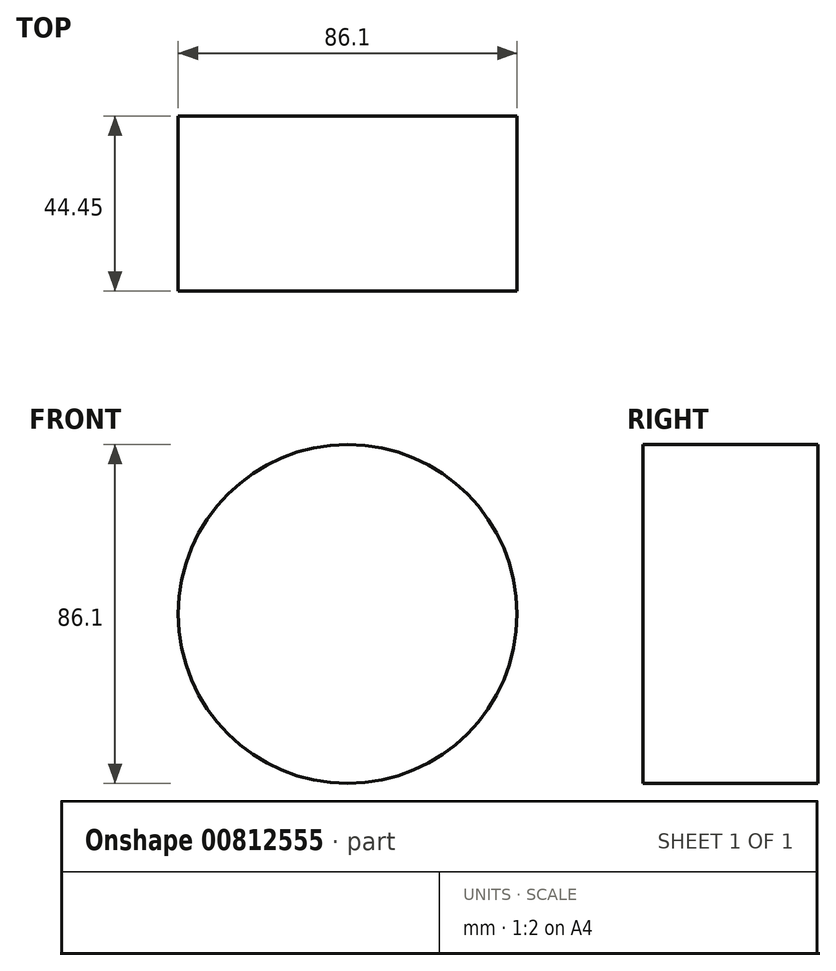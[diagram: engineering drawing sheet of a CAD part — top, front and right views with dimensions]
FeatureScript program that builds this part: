
annotation { "Feature Type Name" : "Feature", "Feature Type Description" : "" }
export const myFeature = defineFeature(function(context is Context, id is Id, definition is map)
    precondition{}
    {
        {
            var Q0;
            Q0=qCreatedBy(makeId("Front.planeOp"),FACE);
            var sketch = newSketch(context, id + "F0", { "sketchPlane" : qUnion([Q0])});
            skCircle(sketch, "E0", {"center": v(0, 0) * mm, "radius": 43.05 * mm});
            skSolve(sketch);
        }
        {
            var Q0;
            Q0=makeQuery(id+"F0.imprint","IMPRINT",FACE,{"disambiguationData":[TD([[makeQuery(id+"F0.imprint","IMPRINT",EDGE,{"derivedFrom":sQuery(id+"F0.wireOp",EDGE,"E0")}),1.0]])]});
            extrude(context, id + "F1", {"entities" : qUnion([Q0]), "depth" : 44.45 * mm, "offsetDistance" : 25.4 * mm});
        }
    });
